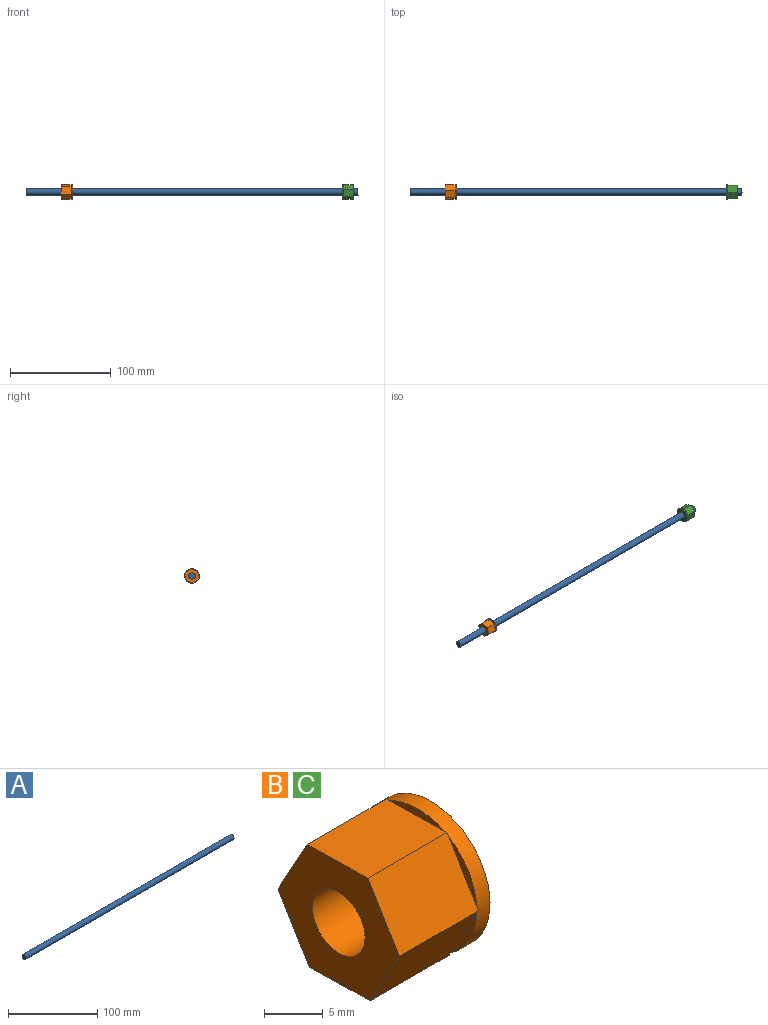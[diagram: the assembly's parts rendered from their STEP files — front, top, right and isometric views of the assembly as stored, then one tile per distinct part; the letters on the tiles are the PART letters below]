
ASSEMBLY  parts=3 mates=2
PART A: 3 faces, bbox 330.2x6.4x6.4 mm
  f0: cylinder r=3.17mm len=330.2mm, axis (-1,0,0), area 6587.2mm2, adj f1,f2
  f1: plane 6.35x6.35mm, normal (1,0,0), area 31.7mm2, adj f0
  f2: plane 6.35x6.35mm, normal (-1,0,0), area 31.7mm2, adj f0
PART B: 22 faces, bbox 11.1x14.7x14.3 mm
  f0: plane 0.6x0.34mm, normal (1,0,0), area 0.1mm2, adj f5,f10,f19
  f1: plane 0.68x0.2mm, normal (1,0,0), area 0.1mm2, adj f5,f6,f19
  f2: plane 0.58x0.35mm, normal (1,0,0), area 0.1mm2, adj f6,f7,f19
  f3: plane 0.6x0.34mm, normal (1,0,0), area 0.1mm2, adj f7,f8,f19
  f4: plane 0.68x0.2mm, normal (1,0,0), area 0.1mm2, adj f8,f9,f19
  f5: plane 9.53x6.27mm, normal (0,0.86,-0.52), area 69.8mm2, adj f0,f1,f6,f10,f13,f14
  f6: plane 9.53x6.43mm, normal (0,0.88,0.48), area 69.8mm2, adj f1,f2,f5,f7,f13,f15
  f7: plane 9.53x7.33mm, normal (0,0.02,1), area 69.8mm2, adj f2,f3,f6,f8,f13,f16
  f8: plane 9.53x6.27mm, normal (0,-0.86,0.52), area 69.8mm2, adj f3,f4,f7,f9,f13,f17
  f9: plane 9.53x6.43mm, normal (0,-0.88,-0.48), area 69.8mm2, adj f4,f8,f10,f12,f13,f18
  f10: plane 9.53x7.33mm, normal (0,-0.02,-1), area 69.8mm2, adj f0,f5,f9,f12,f13,f21
  f11: cylinder r=3.17mm len=11.11mm, axis (-1,0,0), area 221.7mm2, adj f13,f20
  f12: plane 0.58x0.35mm, normal (1,0,0), area 0.1mm2, adj f9,f10,f19
  f13: plane 14.66x12.85mm, normal (-1,0,0), area 108mm2, adj f5,f6,f7,f8,f9,f10,f11
  f14: plane 5.6x3.39mm, normal (-1,0,0), area 3.5mm2, adj f5,f19
  f15: plane 5.74x3.15mm, normal (-1,0,0), area 3.5mm2, adj f6,f19
  f16: plane 6.54x0.86mm, normal (-1,0,0), area 3.5mm2, adj f7,f19
  f17: plane 5.6x3.39mm, normal (-1,0,0), area 3.5mm2, adj f8,f19
  f18: plane 5.74x3.15mm, normal (-1,0,0), area 3.5mm2, adj f9,f19
  f19: cylinder r=7.14mm len=14.29mm, axis (-1,0,0), area 71.3mm2, adj f0,f1,f2,f3,f4,f12,f14,f15
  f20: plane 14.29x14.29mm, normal (1,0,0), area 128.7mm2, adj f11,f19
  f21: plane 6.54x0.86mm, normal (-1,0,0), area 3.5mm2, adj f10,f19
PART C: same geometry as B
PLACE A rot(axis=(-1,0,0),39.3deg) t=(-1349.42,1048.08,-5923.06)mm
PLACE B rot(axis=(-1,0,0),42.8deg) t=(-1314.17,640.79,-5935.3)mm
PLACE C rot(axis=(0,0.98,-0.21),180deg) t=(-1023.98,4775.05,246.02)mm
MATE cylindrical A.f0 <-> B.f11  axis (-1,0,0) through (-1349.42,-923.63,-415.75)mm
MATE revolute A.f0 <-> C.f11  axis (1,0,0) through (-1019.22,-923.63,-415.75)mm
